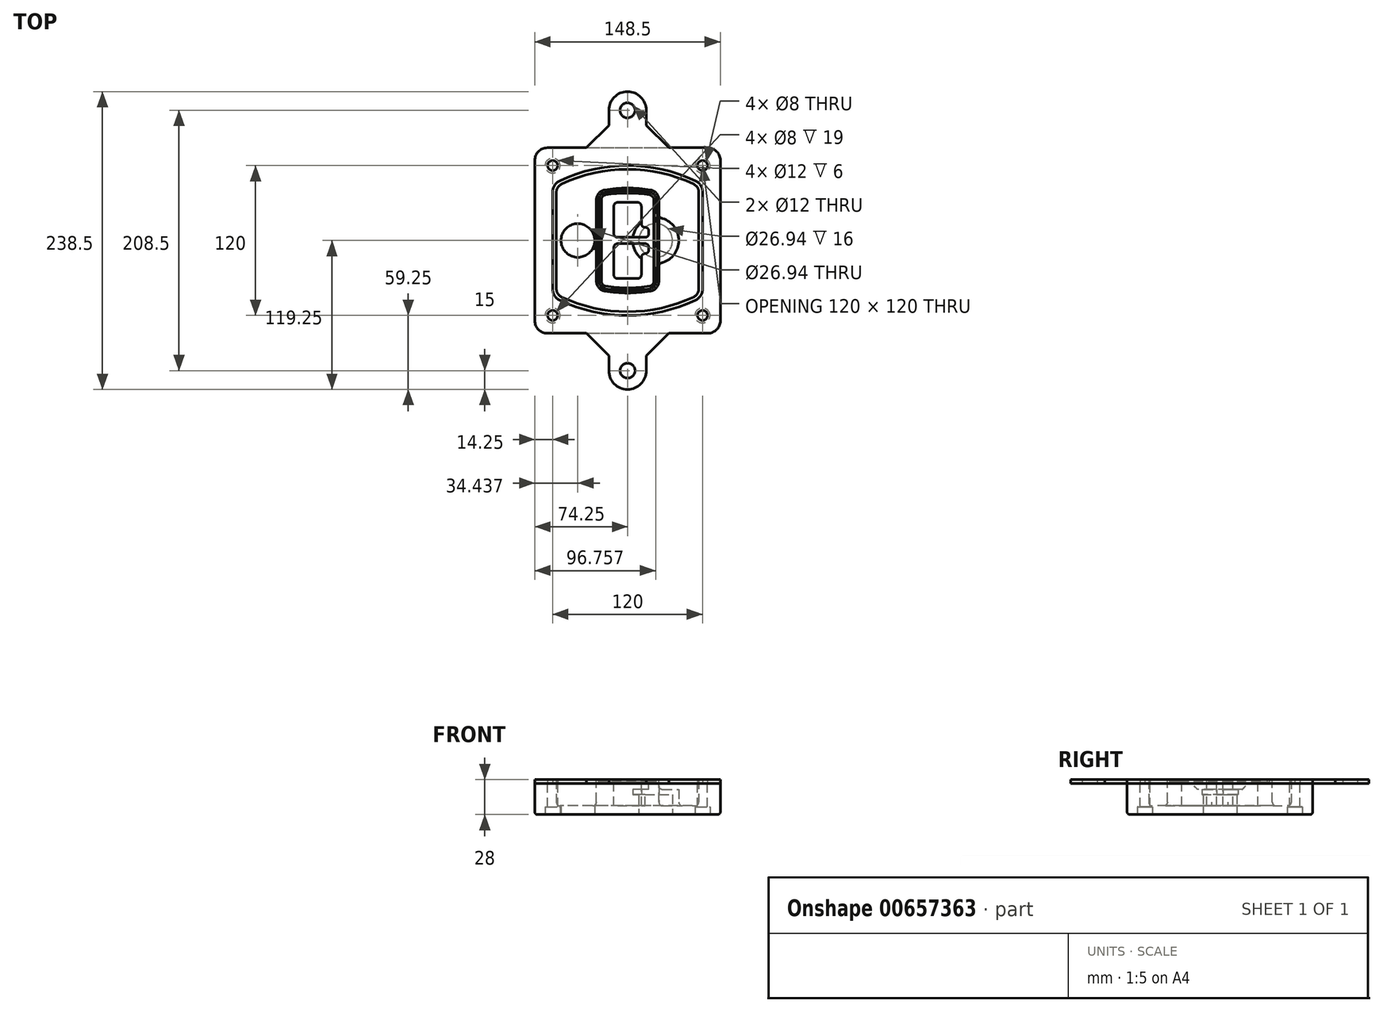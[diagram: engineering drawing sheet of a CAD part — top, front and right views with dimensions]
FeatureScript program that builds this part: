
annotation { "Feature Type Name" : "Feature", "Feature Type Description" : "" }
export const myFeature = defineFeature(function(context is Context, id is Id, definition is map)
    precondition{}
    {
        {
            var Q0;
            Q0=qCreatedBy(makeId("Top.planeOp"),FACE);
            var sketch = newSketch(context, id + "F0", { "sketchPlane" : qUnion([Q0])});
            skPoint(sketch, "E0.rect.middle", {"position": v(0, 0) * mm});
            skLineSegment(sketch, "E1.bottom", {"start": v(-64.25, -74.25) * mm, "end": v(64.25, -74.25) * mm});
            skLineSegment(sketch, "E1.top", {"start": v(-64.25, 74.25) * mm, "end": v(64.25, 74.25) * mm});
            skLineSegment(sketch, "E1.left", {"start": v(-74.25, -64.25) * mm, "end": v(-74.25, 64.25) * mm});
            skLineSegment(sketch, "E1.right", {"start": v(74.25, -64.25) * mm, "end": v(74.25, 64.25) * mm});
            skLineSegment(sketch, "E2", {"start": v(-74.25, 74.25) * mm, "end": v(74.25, -74.25) * mm, "construction": true});
            skLineSegment(sketch, "E3", {"start": v(74.25, 74.25) * mm, "end": v(-74.25, -74.25) * mm, "construction": true});
            skCircle(sketch, "E4", {"center": v(-60, 60) * mm, "radius": 4 * mm});
            skCircle(sketch, "E5", {"center": v(60, 60) * mm, "radius": 4 * mm});
            skCircle(sketch, "E6", {"center": v(60, -60) * mm, "radius": 4 * mm});
            skCircle(sketch, "E7", {"center": v(-60, -60) * mm, "radius": 4 * mm});
            skLineSegment(sketch, "E8", {"start": v(-60, 60) * mm, "end": v(60, 60) * mm, "construction": true});
            skLineSegment(sketch, "E9", {"start": v(60, 60) * mm, "end": v(60, -60) * mm, "construction": true});
            skLineSegment(sketch, "E10", {"start": v(60, -60) * mm, "end": v(-60, -60) * mm, "construction": true});
            skLineSegment(sketch, "E11", {"start": v(-60, -60) * mm, "end": v(-60, 60) * mm, "construction": true});
            skLineSegment(sketch, "E12", {"start": v(-60, 38.83) * mm, "end": v(-60, -38.83) * mm});
            skLineSegment(sketch, "E13", {"start": v(60, 38.83) * mm, "end": v(60, -38.83) * mm});
            skArc(sketch, "E14", {"start": v(54.26, 47.88) * mm, "mid": v(0, 60) * mm, "end": v(-54.26, 47.88) * mm});
            skArc(sketch, "E15", {"start": v(-54.26, -47.88) * mm, "mid": v(0, -60) * mm, "end": v(54.26, -47.88) * mm});
            skLineSegment(sketch, "E16", {"start": v(-60, 0) * mm, "end": v(60, 0) * mm, "construction": true});
            skPoint(sketch, "E17.visualSharp", {"position": v(-60, -45) * mm});
            skArc(sketch, "E17.filletArc", {"start": v(-60, -38.83) * mm, "mid": v(-58.44, -44.2) * mm, "end": v(-54.26, -47.88) * mm});
            skPoint(sketch, "E18.visualSharp", {"position": v(-60, 45) * mm});
            skArc(sketch, "E18.filletArc", {"start": v(-54.26, 47.88) * mm, "mid": v(-58.44, 44.2) * mm, "end": v(-60, 38.83) * mm});
            skPoint(sketch, "E19.visualSharp", {"position": v(60, 45) * mm});
            skArc(sketch, "E19.filletArc", {"start": v(60, 38.83) * mm, "mid": v(58.44, 44.2) * mm, "end": v(54.26, 47.88) * mm});
            skPoint(sketch, "E20.visualSharp", {"position": v(60, -45) * mm});
            skArc(sketch, "E20.filletArc", {"start": v(54.26, -47.88) * mm, "mid": v(58.44, -44.2) * mm, "end": v(60, -38.83) * mm});
            skPoint(sketch, "E21.visualSharp", {"position": v(-74.25, 74.25) * mm});
            skArc(sketch, "E21.filletArc", {"start": v(-64.25, 74.25) * mm, "mid": v(-71.32, 71.32) * mm, "end": v(-74.25, 64.25) * mm});
            skPoint(sketch, "E22.visualSharp", {"position": v(74.25, 74.25) * mm});
            skArc(sketch, "E22.filletArc", {"start": v(74.25, 64.25) * mm, "mid": v(71.32, 71.32) * mm, "end": v(64.25, 74.25) * mm});
            skPoint(sketch, "E23.visualSharp", {"position": v(74.25, -74.25) * mm});
            skArc(sketch, "E23.filletArc", {"start": v(64.25, -74.25) * mm, "mid": v(71.32, -71.32) * mm, "end": v(74.25, -64.25) * mm});
            skPoint(sketch, "E24.visualSharp", {"position": v(-74.25, -74.25) * mm});
            skArc(sketch, "E24.filletArc", {"start": v(-74.25, -64.25) * mm, "mid": v(-71.32, -71.32) * mm, "end": v(-64.25, -74.25) * mm});
            skArc(sketch, "E25.0", {"start": v(57, 38.83) * mm, "mid": v(55.9, 42.58) * mm, "end": v(52.98, 45.17) * mm});
            skLineSegment(sketch, "E25.1", {"start": v(57, 38.83) * mm, "end": v(57, -38.83) * mm});
            skArc(sketch, "E25.2", {"start": v(52.98, -45.17) * mm, "mid": v(55.9, -42.58) * mm, "end": v(57, -38.83) * mm});
            skArc(sketch, "E25.3", {"start": v(-52.98, -45.17) * mm, "mid": v(0, -57) * mm, "end": v(52.98, -45.17) * mm});
            skArc(sketch, "E25.4", {"start": v(-57, -38.83) * mm, "mid": v(-55.9, -42.58) * mm, "end": v(-52.98, -45.17) * mm});
            skArc(sketch, "E25.5", {"start": v(52.98, 45.17) * mm, "mid": v(0, 57) * mm, "end": v(-52.98, 45.17) * mm});
            skLineSegment(sketch, "E25.6", {"start": v(-57, 38.83) * mm, "end": v(-57, -38.83) * mm});
            skArc(sketch, "E25.7", {"start": v(-52.98, 45.17) * mm, "mid": v(-55.9, 42.58) * mm, "end": v(-57, 38.83) * mm});
            skArc(sketch, "E26.0", {"start": v(-55.96, 51.5) * mm, "mid": v(-61.82, 46.33) * mm, "end": v(-64, 38.83) * mm});
            skArc(sketch, "E26.1", {"start": v(55.96, 51.5) * mm, "mid": v(0, 64) * mm, "end": v(-55.96, 51.5) * mm});
            skArc(sketch, "E26.2", {"start": v(64, 38.83) * mm, "mid": v(61.82, 46.33) * mm, "end": v(55.96, 51.5) * mm});
            skLineSegment(sketch, "E26.3", {"start": v(64, 38.83) * mm, "end": v(64, -38.83) * mm});
            skArc(sketch, "E26.4", {"start": v(55.96, -51.5) * mm, "mid": v(61.82, -46.33) * mm, "end": v(64, -38.83) * mm});
            skLineSegment(sketch, "E26.5", {"start": v(-64, 38.83) * mm, "end": v(-64, -38.83) * mm});
            skArc(sketch, "E26.6", {"start": v(-55.96, -51.5) * mm, "mid": v(0, -64) * mm, "end": v(55.96, -51.5) * mm});
            skArc(sketch, "E26.7", {"start": v(-64, -38.83) * mm, "mid": v(-61.82, -46.33) * mm, "end": v(-55.96, -51.5) * mm});
            skLineSegment(sketch, "E27", {"start": v(0, 74.25) * mm, "end": v(0, 104.25) * mm, "construction": true});
            skCircle(sketch, "E28", {"center": v(0, 104.25) * mm, "radius": 6 * mm});
            skArc(sketch, "E29", {"start": v(-15, 104.25) * mm, "mid": v(0, 119.25) * mm, "end": v(15, 104.25) * mm});
            skLineSegment(sketch, "E30", {"start": v(-15, 104.25) * mm, "end": v(-15, 92.25) * mm});
            skLineSegment(sketch, "E31", {"start": v(15, 104.25) * mm, "end": v(15, 92.25) * mm});
            skLineSegment(sketch, "E32", {"start": v(15, 92.25) * mm, "end": v(33, 74.25) * mm});
            skLineSegment(sketch, "E33", {"start": v(-15, 92.25) * mm, "end": v(-33, 74.25) * mm});
            skCircle(sketch, "E34", {"center": v(0, -104.25) * mm, "radius": 6 * mm});
            skArc(sketch, "E35", {"start": v(15, -104.25) * mm, "mid": v(0, -119.25) * mm, "end": v(-15, -104.25) * mm});
            skLineSegment(sketch, "E36", {"start": v(-15, -104.25) * mm, "end": v(-15, -92.25) * mm});
            skLineSegment(sketch, "E37", {"start": v(15, -104.25) * mm, "end": v(15, -85.72) * mm});
            skLineSegment(sketch, "E38", {"start": v(15, -92.25) * mm, "end": v(33, -74.25) * mm});
            skLineSegment(sketch, "E39", {"start": v(-15, -92.25) * mm, "end": v(-33, -74.25) * mm});
            skLineSegment(sketch, "E40", {"start": v(0, -104.25) * mm, "end": v(0, -74.25) * mm, "construction": true});
            skSolve(sketch);
        }
        {
            var Q0;
            Q0=makeQuery(id+"F0.imprint","IMPRINT",FACE,{"disambiguationData":[TD([[makeQuery(id+"F0.imprint","IMPRINT",EDGE,{"derivedFrom":sQuery(id+"F0.wireOp",EDGE,"E1.bottom")}),1.0]])]});
            var Q1;
            Q1=makeQuery(id+"F0.imprint","IMPRINT",FACE,{"disambiguationData":[TD([[makeQuery(id+"F0.imprint","IMPRINT",EDGE,{"derivedFrom":sQuery(id+"F0.wireOp",EDGE,"E12")}),1.0]])]});
            var Q2;
            Q2=makeQuery(id+"F0.imprint","IMPRINT",FACE,{"disambiguationData":[TD([[makeQuery(id+"F0.imprint","IMPRINT",EDGE,{"derivedFrom":sQuery(id+"F0.wireOp",EDGE,"E25.0")}),1.0]])]});
            var Q3;
            Q3=makeQuery(id+"F0.imprint","IMPRINT",FACE,{"disambiguationData":[TD([[makeQuery(id+"F0.imprint","IMPRINT",EDGE,{"derivedFrom":sQuery(id+"F0.wireOp",EDGE,"E12")}),-1.0]])]});
            extrude(context, id + "F1", {"entities" : qUnion([Q0, Q1, Q2, Q3]), "oppositeDirection" : true, "depth" : 25 * mm});
        }
        {
            var Q0;
            Q0=makeQuery(id+"F0.imprint","IMPRINT",FACE,{"disambiguationData":[TD([[makeQuery(id+"F0.imprint","IMPRINT",EDGE,{"derivedFrom":sQuery(id+"F0.wireOp",EDGE,"E12")}),1.0]])]});
            extrude(context, id + "F2", {"entities" : qUnion([Q0]), "operationType" : NewBodyOperationType.ADD, "depth" : 3 * mm});
        }
        {
            var Q0;
            Q0=makeQuery(id+"F0.imprint","IMPRINT",FACE,{"disambiguationData":[TD([[makeQuery(id+"F0.imprint","IMPRINT",EDGE,{"derivedFrom":sQuery(id+"F0.wireOp",EDGE,"E25.0")}),1.0]])]});
            extrude(context, id + "F3", {"entities" : qUnion([Q0]), "operationType" : NewBodyOperationType.REMOVE, "oppositeDirection" : true, "depth" : 18 * mm});
        }
        {
            var Q0;
            Q0=makeQuery(id+"F2.opExtrude","CAP_FACE",FACE,{"disambiguationData":[OSD([sQuery(id+"F0.wireOp",EDGE,"E12"),sQuery(id+"F0.wireOp",EDGE,"E13"),sQuery(id+"F0.wireOp",EDGE,"E14"),sQuery(id+"F0.wireOp",EDGE,"E15"),sQuery(id+"F0.wireOp",EDGE,"E17.filletArc"),sQuery(id+"F0.wireOp",EDGE,"E18.filletArc"),sQuery(id+"F0.wireOp",EDGE,"E19.filletArc"),sQuery(id+"F0.wireOp",EDGE,"E20.filletArc"),sQuery(id+"F0.wireOp",EDGE,"E25.0"),sQuery(id+"F0.wireOp",EDGE,"E25.1"),sQuery(id+"F0.wireOp",EDGE,"E25.2"),sQuery(id+"F0.wireOp",EDGE,"E25.3"),sQuery(id+"F0.wireOp",EDGE,"E25.4"),sQuery(id+"F0.wireOp",EDGE,"E25.5"),sQuery(id+"F0.wireOp",EDGE,"E25.6"),sQuery(id+"F0.wireOp",EDGE,"E25.7")])],"isStart":false});
            var sketch = newSketch(context, id + "F4", { "sketchPlane" : qUnion([Q0])});
            skArc(sketch, "E41.0", {"start": v(-18.34, -40.45) * mm, "mid": v(0, -42) * mm, "end": v(18.34, -40.45) * mm});
            skArc(sketch, "E42.0", {"start": v(18.34, 40.45) * mm, "mid": v(0, 42) * mm, "end": v(-18.34, 40.45) * mm});
            skLineSegment(sketch, "E43", {"start": v(-25, 32.57) * mm, "end": v(-25, -32.57) * mm});
            skLineSegment(sketch, "E44", {"start": v(25, 32.57) * mm, "end": v(25, -32.57) * mm});
            skLineSegment(sketch, "E45", {"start": v(-25, 39.1) * mm, "end": v(25, 39.1) * mm, "construction": true});
            skLineSegment(sketch, "E46", {"start": v(-25, -39.1) * mm, "end": v(25, -39.1) * mm, "construction": true});
            skPoint(sketch, "E47.visualSharp", {"position": v(-25, 39.1) * mm});
            skArc(sketch, "E47.filletArc", {"start": v(-18.34, 40.45) * mm, "mid": v(-23.11, 37.73) * mm, "end": v(-25, 32.57) * mm});
            skPoint(sketch, "E48.visualSharp", {"position": v(25, 39.1) * mm});
            skArc(sketch, "E48.filletArc", {"start": v(25, 32.57) * mm, "mid": v(23.11, 37.73) * mm, "end": v(18.34, 40.45) * mm});
            skPoint(sketch, "E49.visualSharp", {"position": v(25, -39.1) * mm});
            skArc(sketch, "E49.filletArc", {"start": v(18.34, -40.45) * mm, "mid": v(23.11, -37.73) * mm, "end": v(25, -32.57) * mm});
            skPoint(sketch, "E50.visualSharp", {"position": v(-25, -39.1) * mm});
            skArc(sketch, "E50.filletArc", {"start": v(-25, -32.57) * mm, "mid": v(-23.11, -37.73) * mm, "end": v(-18.34, -40.45) * mm});
            skArc(sketch, "E51.0", {"start": v(52.98, 45.17) * mm, "mid": v(0, 57) * mm, "end": v(-52.98, 45.17) * mm});
            skArc(sketch, "E51.1", {"start": v(-52.98, 45.17) * mm, "mid": v(-55.9, 42.58) * mm, "end": v(-57, 38.83) * mm});
            skLineSegment(sketch, "E51.2", {"start": v(-57, 38.83) * mm, "end": v(-57, -38.83) * mm});
            skArc(sketch, "E51.3", {"start": v(-57, -38.83) * mm, "mid": v(-55.9, -42.58) * mm, "end": v(-52.98, -45.17) * mm});
            skArc(sketch, "E51.4", {"start": v(-52.98, -45.17) * mm, "mid": v(0, -57) * mm, "end": v(52.98, -45.17) * mm});
            skArc(sketch, "E51.5", {"start": v(52.98, -45.17) * mm, "mid": v(55.9, -42.58) * mm, "end": v(57, -38.83) * mm});
            skLineSegment(sketch, "E51.6", {"start": v(57, 38.83) * mm, "end": v(57, -38.83) * mm});
            skArc(sketch, "E51.7", {"start": v(57, 38.83) * mm, "mid": v(55.9, 42.58) * mm, "end": v(52.98, 45.17) * mm});
            skLineSegment(sketch, "E52.0", {"start": v(23, 32.57) * mm, "end": v(23, -32.57) * mm});
            skArc(sketch, "E52.1", {"start": v(18, -38.48) * mm, "mid": v(21.58, -36.44) * mm, "end": v(23, -32.57) * mm});
            skArc(sketch, "E52.2", {"start": v(-18, -38.48) * mm, "mid": v(0, -40) * mm, "end": v(18, -38.48) * mm});
            skArc(sketch, "E52.3", {"start": v(-23, -32.57) * mm, "mid": v(-21.58, -36.44) * mm, "end": v(-18, -38.48) * mm});
            skLineSegment(sketch, "E52.4", {"start": v(-23, 32.57) * mm, "end": v(-23, -32.57) * mm});
            skArc(sketch, "E52.5", {"start": v(23, 32.57) * mm, "mid": v(21.58, 36.44) * mm, "end": v(18, 38.48) * mm});
            skArc(sketch, "E52.6", {"start": v(-18, 38.48) * mm, "mid": v(-21.58, 36.44) * mm, "end": v(-23, 32.57) * mm});
            skArc(sketch, "E52.7", {"start": v(18, 38.48) * mm, "mid": v(0, 40) * mm, "end": v(-18, 38.48) * mm});
            skArc(sketch, "E53.0", {"start": v(21, 32.57) * mm, "mid": v(20.06, 35.15) * mm, "end": v(17.67, 36.5) * mm});
            skLineSegment(sketch, "E53.1", {"start": v(21, 32.57) * mm, "end": v(21, -32.57) * mm});
            skArc(sketch, "E53.2", {"start": v(17.67, -36.5) * mm, "mid": v(20.06, -35.15) * mm, "end": v(21, -32.57) * mm});
            skArc(sketch, "E53.3", {"start": v(-17.67, -36.5) * mm, "mid": v(0, -38) * mm, "end": v(17.67, -36.5) * mm});
            skArc(sketch, "E53.4", {"start": v(-21, -32.57) * mm, "mid": v(-20.06, -35.15) * mm, "end": v(-17.67, -36.5) * mm});
            skArc(sketch, "E53.5", {"start": v(17.67, 36.5) * mm, "mid": v(0, 38) * mm, "end": v(-17.67, 36.5) * mm});
            skLineSegment(sketch, "E53.6", {"start": v(-21, 32.57) * mm, "end": v(-21, -32.57) * mm});
            skArc(sketch, "E53.7", {"start": v(-17.67, 36.5) * mm, "mid": v(-20.06, 35.15) * mm, "end": v(-21, 32.57) * mm});
            skLineSegment(sketch, "E54", {"start": v(-25, 0) * mm, "end": v(25, 0) * mm, "construction": true});
            skLineSegment(sketch, "E55", {"start": v(-11, 5.5) * mm, "end": v(-11, 27.5) * mm});
            skLineSegment(sketch, "E56", {"start": v(-8, 30.5) * mm, "end": v(8, 30.5) * mm});
            skLineSegment(sketch, "E57", {"start": v(11, 27.5) * mm, "end": v(11, 13.5) * mm});
            skLineSegment(sketch, "E58", {"start": v(14, 10.5) * mm, "end": v(14, 10.5) * mm});
            skLineSegment(sketch, "E59", {"start": v(17, 7.5) * mm, "end": v(17, 5.5) * mm});
            skLineSegment(sketch, "E60", {"start": v(14, 2.5) * mm, "end": v(-8, 2.5) * mm});
            skPoint(sketch, "E61.visualSharp", {"position": v(-11, 30.5) * mm});
            skArc(sketch, "E61.filletArc", {"start": v(-8, 30.5) * mm, "mid": v(-10.12, 29.62) * mm, "end": v(-11, 27.5) * mm});
            skPoint(sketch, "E62.visualSharp", {"position": v(11, 30.5) * mm});
            skArc(sketch, "E62.filletArc", {"start": v(11, 27.5) * mm, "mid": v(10.12, 29.62) * mm, "end": v(8, 30.5) * mm});
            skPoint(sketch, "E63.visualSharp", {"position": v(11, 10.5) * mm});
            skArc(sketch, "E63.filletArc", {"start": v(11, 13.5) * mm, "mid": v(11.88, 11.38) * mm, "end": v(14, 10.5) * mm});
            skPoint(sketch, "E64.visualSharp", {"position": v(17, 10.5) * mm});
            skArc(sketch, "E64.filletArc", {"start": v(17, 7.5) * mm, "mid": v(16.12, 9.62) * mm, "end": v(14, 10.5) * mm});
            skPoint(sketch, "E65.visualSharp", {"position": v(17, 2.5) * mm});
            skArc(sketch, "E65.filletArc", {"start": v(14, 2.5) * mm, "mid": v(16.12, 3.38) * mm, "end": v(17, 5.5) * mm});
            skPoint(sketch, "E66.visualSharp", {"position": v(-11, 2.5) * mm});
            skArc(sketch, "E66.filletArc", {"start": v(-11, 5.5) * mm, "mid": v(-10.12, 3.38) * mm, "end": v(-8, 2.5) * mm});
            skLineSegment(sketch, "E67.0.MirrorCS", {"start": v(14, -2.5) * mm, "end": v(-8, -2.5) * mm});
            skArc(sketch, "E68.0.MirrorCS", {"start": v(-11, -5.5) * mm, "mid": v(-10.12, -3.38) * mm, "end": v(-8, -2.5) * mm});
            skLineSegment(sketch, "E69.0.MirrorCS", {"start": v(-11, -5.5) * mm, "end": v(-11, -27.5) * mm});
            skArc(sketch, "E70.0.MirrorCS", {"start": v(-8, -30.5) * mm, "mid": v(-10.12, -29.62) * mm, "end": v(-11, -27.5) * mm});
            skLineSegment(sketch, "E71.0.MirrorCS", {"start": v(-8, -30.5) * mm, "end": v(8, -30.5) * mm});
            skArc(sketch, "E72.0.MirrorCS", {"start": v(11, -27.5) * mm, "mid": v(10.12, -29.62) * mm, "end": v(8, -30.5) * mm});
            skLineSegment(sketch, "E73.0.MirrorCS", {"start": v(11, -27.5) * mm, "end": v(11, -13.5) * mm});
            skArc(sketch, "E74.0.MirrorCS", {"start": v(11, -13.5) * mm, "mid": v(11.88, -11.38) * mm, "end": v(14, -10.5) * mm});
            skArc(sketch, "E75.0.MirrorCS", {"start": v(17, -7.5) * mm, "mid": v(16.12, -9.62) * mm, "end": v(14, -10.5) * mm});
            skLineSegment(sketch, "E76.0.MirrorCS", {"start": v(17, -7.5) * mm, "end": v(17, -5.5) * mm});
            skArc(sketch, "E77.0.MirrorCS", {"start": v(14, -2.5) * mm, "mid": v(16.12, -3.38) * mm, "end": v(17, -5.5) * mm});
            skSolve(sketch);
        }
        {
            var Q0;
            Q0=makeQuery(id+"F4.imprint","IMPRINT",FACE,{"disambiguationData":[TD([[makeQuery(id+"F4.imprint","IMPRINT",EDGE,{"derivedFrom":sQuery(id+"F4.wireOp",EDGE,"E41.0")}),1.0]])]});
            var Q1;
            Q1=makeQuery(id+"F4.imprint","IMPRINT",FACE,{"disambiguationData":[TD([[makeQuery(id+"F4.imprint","IMPRINT",EDGE,{"derivedFrom":sQuery(id+"F4.wireOp",EDGE,"E52.0")}),-1.0]])]});
            var Q2;
            Q2=makeQuery(id+"F4.imprint","IMPRINT",FACE,{"disambiguationData":[TD([[makeQuery(id+"F4.imprint","IMPRINT",EDGE,{"derivedFrom":sQuery(id+"F4.wireOp",EDGE,"E53.0")}),1.0]])]});
            extrude(context, id + "F5", {"entities" : qUnion([Q0, Q1, Q2]), "operationType" : NewBodyOperationType.ADD, "endBound" : BoundingType.UP_TO_NEXT, "oppositeDirection" : true, "depth" : 25 * mm});
        }
        {
            var Q0;
            Q0=makeQuery(id+"F4.imprint","IMPRINT",FACE,{"disambiguationData":[TD([[makeQuery(id+"F4.imprint","IMPRINT",EDGE,{"derivedFrom":sQuery(id+"F4.wireOp",EDGE,"E52.0")}),-1.0]])]});
            extrude(context, id + "F6", {"entities" : qUnion([Q0]), "operationType" : NewBodyOperationType.REMOVE, "oppositeDirection" : true, "depth" : 2 * mm});
        }
        {
            var Q0;
            Q0=makeQuery(id+"F1.opExtrude","CAP_FACE",FACE,{"disambiguationData":[OSD([sQuery(id+"F0.wireOp",EDGE,"E1.bottom"),sQuery(id+"F0.wireOp",EDGE,"E1.top"),sQuery(id+"F0.wireOp",EDGE,"E1.left"),sQuery(id+"F0.wireOp",EDGE,"E1.right"),sQuery(id+"F0.wireOp",EDGE,"E4"),sQuery(id+"F0.wireOp",EDGE,"E5"),sQuery(id+"F0.wireOp",EDGE,"E6"),sQuery(id+"F0.wireOp",EDGE,"E7"),sQuery(id+"F0.wireOp",EDGE,"E21.filletArc"),sQuery(id+"F0.wireOp",EDGE,"E22.filletArc"),sQuery(id+"F0.wireOp",EDGE,"E23.filletArc"),sQuery(id+"F0.wireOp",EDGE,"E24.filletArc")])],"isStart":false});
            var sketch = newSketch(context, id + "F7", { "sketchPlane" : qUnion([Q0])});
            skCircle(sketch, "E78", {"center": v(22.5, 0) * mm, "radius": 13.47 * mm});
            skCircle(sketch, "E79", {"center": v(-39.81, 0) * mm, "radius": 13.47 * mm});
            skLineSegment(sketch, "E80", {"start": v(74.25, 0) * mm, "end": v(-74.25, 0) * mm});
            skCircle(sketch, "E81", {"center": v(22.5, 0) * mm, "radius": 18.47 * mm});
            skCircle(sketch, "E82", {"center": v(60, -60) * mm, "radius": 6 * mm});
            skCircle(sketch, "E83", {"center": v(-60, -60) * mm, "radius": 6 * mm});
            skCircle(sketch, "E84", {"center": v(-60, 60) * mm, "radius": 6 * mm});
            skCircle(sketch, "E85", {"center": v(60, 60) * mm, "radius": 6 * mm});
            skSolve(sketch);
        }
        {
            var Q0;
            {var subQ1=sQuery(id+"F7.wireOp",EDGE,"E80");var subQ4=sQuery(id+"F7.wireOp",EDGE,"E78");var subQ6=makeQuery(id+"F7.imprint","INTERSECT",VERTEX,{"disambiguationData":[OD(0.0)],"derivedFrom":[subQ4,subQ1]});Q0=makeQuery(id+"F7.imprint","IMPRINT",FACE,{"disambiguationData":[TD([[makeQuery(id+"F7.imprint","IMPRINT",EDGE,{"disambiguationData":[TD([[subQ6,-1.0]])],"derivedFrom":subQ4}),-1.0]])]});}
            var Q1;
            {var subQ0=sQuery(id+"F7.wireOp",EDGE,"E80");var subQ1=sQuery(id+"F7.wireOp",EDGE,"E78");var subQ3=makeQuery(id+"F7.imprint","INTERSECT",VERTEX,{"disambiguationData":[OD(0.0)],"derivedFrom":[subQ1,subQ0]});Q1=makeQuery(id+"F7.imprint","IMPRINT",FACE,{"disambiguationData":[TD([[makeQuery(id+"F7.imprint","IMPRINT",EDGE,{"disambiguationData":[TD([[subQ3,-1.0]])],"derivedFrom":subQ1}),1.0]])]});}
            var Q2;
            {var subQ0=sQuery(id+"F7.wireOp",EDGE,"E80");var subQ1=sQuery(id+"F7.wireOp",EDGE,"E78");var subQ3=makeQuery(id+"F7.imprint","INTERSECT",VERTEX,{"disambiguationData":[OD(0.0)],"derivedFrom":[subQ1,subQ0]});Q2=makeQuery(id+"F7.imprint","IMPRINT",FACE,{"disambiguationData":[TD([[makeQuery(id+"F7.imprint","IMPRINT",EDGE,{"disambiguationData":[TD([[subQ3,1.0]])],"derivedFrom":subQ1}),1.0]])]});}
            var Q3;
            {var subQ1=sQuery(id+"F7.wireOp",EDGE,"E80");var subQ4=sQuery(id+"F7.wireOp",EDGE,"E78");var subQ6=makeQuery(id+"F7.imprint","INTERSECT",VERTEX,{"disambiguationData":[OD(0.0)],"derivedFrom":[subQ4,subQ1]});Q3=makeQuery(id+"F7.imprint","IMPRINT",FACE,{"disambiguationData":[TD([[makeQuery(id+"F7.imprint","IMPRINT",EDGE,{"disambiguationData":[TD([[subQ6,1.0]])],"derivedFrom":subQ4}),-1.0]])]});}
            extrude(context, id + "F8", {"entities" : qUnion([Q0, Q1, Q2, Q3]), "operationType" : NewBodyOperationType.ADD, "oppositeDirection" : true, "depth" : 20 * mm});
        }
        {
            var Q0;
            {var subQ0=sQuery(id+"F7.wireOp",EDGE,"E80");var subQ1=sQuery(id+"F7.wireOp",EDGE,"E78");var subQ3=makeQuery(id+"F7.imprint","INTERSECT",VERTEX,{"disambiguationData":[OD(0.0)],"derivedFrom":[subQ1,subQ0]});Q0=makeQuery(id+"F7.imprint","IMPRINT",FACE,{"disambiguationData":[TD([[makeQuery(id+"F7.imprint","IMPRINT",EDGE,{"disambiguationData":[TD([[subQ3,-1.0]])],"derivedFrom":subQ1}),1.0]])]});}
            var Q1;
            {var subQ0=sQuery(id+"F7.wireOp",EDGE,"E80");var subQ1=sQuery(id+"F7.wireOp",EDGE,"E78");var subQ3=makeQuery(id+"F7.imprint","INTERSECT",VERTEX,{"disambiguationData":[OD(0.0)],"derivedFrom":[subQ1,subQ0]});Q1=makeQuery(id+"F7.imprint","IMPRINT",FACE,{"disambiguationData":[TD([[makeQuery(id+"F7.imprint","IMPRINT",EDGE,{"disambiguationData":[TD([[subQ3,1.0]])],"derivedFrom":subQ1}),1.0]])]});}
            var Q2;
            Q2 = qSketchRegion(id + "F17", true);
            extrude(context, id + "F9", {"entities" : qUnion([Q0, Q1, Q2]), "operationType" : NewBodyOperationType.REMOVE, "oppositeDirection" : true, "depth" : 16 * mm, "offsetDistance" : 25 * mm});
        }
        {
            var Q0;
            {var subQ0=sQuery(id+"F7.wireOp",EDGE,"E80");var subQ1=sQuery(id+"F7.wireOp",EDGE,"E79");var subQ3=makeQuery(id+"F7.imprint","INTERSECT",VERTEX,{"disambiguationData":[OD(0.0)],"derivedFrom":[subQ1,subQ0]});Q0=makeQuery(id+"F7.imprint","IMPRINT",FACE,{"disambiguationData":[TD([[makeQuery(id+"F7.imprint","IMPRINT",EDGE,{"disambiguationData":[TD([[subQ3,-1.0]])],"derivedFrom":subQ1}),1.0]])]});}
            var Q1;
            {var subQ0=sQuery(id+"F7.wireOp",EDGE,"E80");var subQ1=sQuery(id+"F7.wireOp",EDGE,"E79");var subQ3=makeQuery(id+"F7.imprint","INTERSECT",VERTEX,{"disambiguationData":[OD(0.0)],"derivedFrom":[subQ1,subQ0]});Q1=makeQuery(id+"F7.imprint","IMPRINT",FACE,{"disambiguationData":[TD([[makeQuery(id+"F7.imprint","IMPRINT",EDGE,{"disambiguationData":[TD([[subQ3,1.0]])],"derivedFrom":subQ1}),1.0]])]});}
            extrude(context, id + "F10", {"entities" : qUnion([Q0, Q1]), "operationType" : NewBodyOperationType.REMOVE, "oppositeDirection" : true, "depth" : 25 * mm});
        }
        {
            var Q0;
            Q0=makeQuery(id+"F7.imprint","IMPRINT",FACE,{"disambiguationData":[TD([[makeQuery(id+"F7.imprint","IMPRINT",EDGE,{"derivedFrom":sQuery(id+"F7.wireOp",EDGE,"E82")}),1.0]])]});
            var Q1;
            Q1=makeQuery(id+"F7.imprint","IMPRINT",FACE,{"disambiguationData":[TD([[makeQuery(id+"F7.imprint","IMPRINT",EDGE,{"derivedFrom":makeQuery(id+"F1.opExtrude","CAP_EDGE",EDGE,{"disambiguationData":[OSD([sQuery(id+"F0.wireOp",EDGE,"E5")])],"isStart":false})}),-1.0]])]});
            var Q2;
            Q2=makeQuery(id+"F7.imprint","IMPRINT",FACE,{"disambiguationData":[TD([[makeQuery(id+"F7.imprint","IMPRINT",EDGE,{"derivedFrom":sQuery(id+"F7.wireOp",EDGE,"E83")}),1.0]])]});
            var Q3;
            Q3=makeQuery(id+"F7.imprint","IMPRINT",FACE,{"disambiguationData":[TD([[makeQuery(id+"F7.imprint","IMPRINT",EDGE,{"derivedFrom":makeQuery(id+"F1.opExtrude","CAP_EDGE",EDGE,{"disambiguationData":[OSD([sQuery(id+"F0.wireOp",EDGE,"E4")])],"isStart":false})}),-1.0]])]});
            var Q4;
            Q4=makeQuery(id+"F7.imprint","IMPRINT",FACE,{"disambiguationData":[TD([[makeQuery(id+"F7.imprint","IMPRINT",EDGE,{"derivedFrom":sQuery(id+"F7.wireOp",EDGE,"E84")}),1.0]])]});
            var Q5;
            Q5=makeQuery(id+"F7.imprint","IMPRINT",FACE,{"disambiguationData":[TD([[makeQuery(id+"F7.imprint","IMPRINT",EDGE,{"derivedFrom":makeQuery(id+"F1.opExtrude","CAP_EDGE",EDGE,{"disambiguationData":[OSD([sQuery(id+"F0.wireOp",EDGE,"E7")])],"isStart":false})}),-1.0]])]});
            var Q6;
            Q6=makeQuery(id+"F7.imprint","IMPRINT",FACE,{"disambiguationData":[TD([[makeQuery(id+"F7.imprint","IMPRINT",EDGE,{"derivedFrom":sQuery(id+"F7.wireOp",EDGE,"E85")}),1.0]])]});
            var Q7;
            Q7=makeQuery(id+"F7.imprint","IMPRINT",FACE,{"disambiguationData":[TD([[makeQuery(id+"F7.imprint","IMPRINT",EDGE,{"derivedFrom":makeQuery(id+"F1.opExtrude","CAP_EDGE",EDGE,{"disambiguationData":[OSD([sQuery(id+"F0.wireOp",EDGE,"E6")])],"isStart":false})}),-1.0]])]});
            extrude(context, id + "F11", {"entities" : qUnion([Q0, Q1, Q2, Q3, Q4, Q5, Q6, Q7]), "operationType" : NewBodyOperationType.REMOVE, "oppositeDirection" : true, "depth" : 6 * mm});
        }
        {
            var Q0;
            Q0=makeQuery(id+"F9.boolean.opBoolean","COPY",FACE,{"derivedFrom":makeQuery(id+"F9.opExtrude","CAP_FACE",FACE,{"disambiguationData":[OSD([sQuery(id+"F7.wireOp",EDGE,"E78")])],"isStart":false})});
            var sketch = newSketch(context, id + "F12", { "sketchPlane" : qUnion([Q0])});
            skArc(sketch, "E86.0", {"start": v(11, 14.45) * mm, "mid": v(6.45, 9.13) * mm, "end": v(4.2, 2.5) * mm});
            skArc(sketch, "E86.1", {"start": v(4.2, -2.5) * mm, "mid": v(6.45, -9.13) * mm, "end": v(11, -14.45) * mm});
            skLineSegment(sketch, "E87", {"start": v(4.2, -2.5) * mm, "end": v(14, -2.5) * mm});
            skLineSegment(sketch, "E88.0", {"start": v(14, 2.5) * mm, "end": v(4.2, 2.5) * mm});
            skArc(sketch, "E88.1", {"start": v(14, 2.5) * mm, "mid": v(16.12, 3.38) * mm, "end": v(17, 5.5) * mm});
            skLineSegment(sketch, "E88.2", {"start": v(17, 7.5) * mm, "end": v(17, 5.5) * mm});
            skArc(sketch, "E88.3", {"start": v(17, 7.5) * mm, "mid": v(16.12, 9.62) * mm, "end": v(14, 10.5) * mm});
            skArc(sketch, "E88.4", {"start": v(11, 13.5) * mm, "mid": v(11.88, 11.38) * mm, "end": v(14, 10.5) * mm});
            skLineSegment(sketch, "E88.5", {"start": v(11, 14.45) * mm, "end": v(11, 13.5) * mm});
            skLineSegment(sketch, "E88.7", {"start": v(14, -2.5) * mm, "end": v(4.2, -2.5) * mm});
            skArc(sketch, "E88.8", {"start": v(14, -2.5) * mm, "mid": v(16.12, -3.38) * mm, "end": v(17, -5.5) * mm});
            skLineSegment(sketch, "E88.9", {"start": v(17, -7.5) * mm, "end": v(17, -5.5) * mm});
            skArc(sketch, "E88.10", {"start": v(17, -7.5) * mm, "mid": v(16.12, -9.62) * mm, "end": v(14, -10.5) * mm});
            skArc(sketch, "E88.11", {"start": v(11, -13.5) * mm, "mid": v(11.88, -11.38) * mm, "end": v(14, -10.5) * mm});
            skLineSegment(sketch, "E88.12", {"start": v(11, -14.45) * mm, "end": v(11, -13.5) * mm});
            skPoint(sketch, "E89.orphan", {"position": v(11, -27.5) * mm});
            skPoint(sketch, "E90.orphan", {"position": v(-8, -2.5) * mm});
            skPoint(sketch, "E91.orphan", {"position": v(-8, 2.5) * mm});
            skPoint(sketch, "E92.orphan", {"position": v(11, 27.5) * mm});
            skSolve(sketch);
        }
        {
            var Q0;
            {var subQ7=sQuery(id+"F12.wireOp",EDGE,"E86.0");var subQ14=sQuery(id+"F12.wireOp",EDGE,"E86.1");var subQ16=sQuery(id+"F12.wireOp",EDGE,"E88.1");var subQ18=sQuery(id+"F12.wireOp",EDGE,"E88.8");Q0=qUnion([makeQuery(id+"F12.imprint","IMPRINT",FACE,{"disambiguationData":[TD([[makeQuery(id+"F12.imprint","IMPRINT",EDGE,{"derivedFrom":subQ7}),1.0]])]}),makeQuery(id+"F12.imprint","IMPRINT",FACE,{"disambiguationData":[TD([[makeQuery(id+"F12.imprint","IMPRINT",EDGE,{"derivedFrom":subQ14}),1.0]])]}),makeQuery(id+"F12.imprint","IMPRINT",FACE,{"disambiguationData":[TD([[makeQuery(id+"F12.imprint","IMPRINT",EDGE,{"derivedFrom":subQ16}),1.0]])]}),makeQuery(id+"F12.imprint","IMPRINT",FACE,{"disambiguationData":[TD([[makeQuery(id+"F12.imprint","IMPRINT",EDGE,{"derivedFrom":subQ18}),-1.0]])]})]);}
            var Q1;
            Q1=makeQuery(id+"F5.boolean.opBoolean","SPLIT",FACE,{"disambiguationData":[TD([makeQuery(id+"F5.opExtrude","SWEPT_FACE",FACE,{"disambiguationData":[OSD([sQuery(id+"F4.wireOp",EDGE,"E55")])]})])],"derivedFrom":makeQuery(id+"F3.boolean.opBoolean","COPY",FACE,{"derivedFrom":makeQuery(id+"F3.opExtrude","CAP_FACE",FACE,{"disambiguationData":[OSD([sQuery(id+"F0.wireOp",EDGE,"E25.0"),sQuery(id+"F0.wireOp",EDGE,"E25.1"),sQuery(id+"F0.wireOp",EDGE,"E25.2"),sQuery(id+"F0.wireOp",EDGE,"E25.3"),sQuery(id+"F0.wireOp",EDGE,"E25.4"),sQuery(id+"F0.wireOp",EDGE,"E25.5"),sQuery(id+"F0.wireOp",EDGE,"E25.6"),sQuery(id+"F0.wireOp",EDGE,"E25.7")])],"isStart":false})})});
            extrude(context, id + "F13", {"entities" : qUnion([Q0]), "operationType" : NewBodyOperationType.REMOVE, "endBound" : BoundingType.UP_TO_SURFACE, "endBoundEntityFace" : qUnion([Q1]), "depth" : 25 * mm});
        }
        {
            var Q0;
            Q0=makeQuery(id+"F3.boolean.opBoolean","COPY",EDGE,{"derivedFrom":makeQuery(id+"F3.opExtrude","CAP_EDGE",EDGE,{"disambiguationData":[OSD([sQuery(id+"F0.wireOp",EDGE,"E25.6")])],"isStart":false})});
            var Q1;
            Q1=makeQuery(id+"F8.boolean.opBoolean","INTERSECT",EDGE,{"derivedFrom":[makeQuery(id+"F5.opExtrude","SWEPT_FACE",FACE,{"disambiguationData":[OSD([sQuery(id+"F4.wireOp",EDGE,"E44")])]}),makeQuery(id+"F8.opExtrude","CAP_FACE",FACE,{"disambiguationData":[OSD([sQuery(id+"F7.wireOp",EDGE,"E81")])],"isStart":false})]});
            var Q2;
            Q2=makeQuery(id+"F8.boolean.opBoolean","INTERSECT",EDGE,{"disambiguationData":[OD(1.0)],"derivedFrom":[makeQuery(id+"F5.opExtrude","SWEPT_FACE",FACE,{"disambiguationData":[OSD([sQuery(id+"F4.wireOp",EDGE,"E44")])]}),makeQuery(id+"F8.opExtrude","SWEPT_FACE",FACE,{"disambiguationData":[OSD([sQuery(id+"F7.wireOp",EDGE,"E81")])]})]});
            var Q3;
            {var subQ0=sQuery(id+"F4.wireOp",EDGE,"E44");Q3=makeQuery(id+"F8.boolean.opBoolean","SPLIT",EDGE,{"disambiguationData":[TD([makeQuery(id+"F5.opExtrude","SWEPT_FACE",FACE,{"disambiguationData":[OSD([sQuery(id+"F4.wireOp",EDGE,"E49.filletArc")])]})])],"derivedFrom":makeQuery(id+"F5.opExtrude","CAP_EDGE",EDGE,{"disambiguationData":[OSD([subQ0])],"isStart":false})});}
            var Q4;
            {var subQ0=sQuery(id+"F0.wireOp",EDGE,"E25.7");var subQ1=sQuery(id+"F0.wireOp",EDGE,"E25.1");var subQ2=sQuery(id+"F0.wireOp",EDGE,"E25.6");var subQ3=sQuery(id+"F0.wireOp",EDGE,"E25.5");var subQ4=sQuery(id+"F0.wireOp",EDGE,"E25.4");var subQ5=sQuery(id+"F0.wireOp",EDGE,"E25.0");var subQ6=sQuery(id+"F0.wireOp",EDGE,"E25.2");var subQ7=sQuery(id+"F0.wireOp",EDGE,"E25.3");Q4=makeQuery(id+"F8.boolean.opBoolean","INTERSECT",EDGE,{"derivedFrom":[makeQuery(id+"F5.boolean.opBoolean","SPLIT",FACE,{"disambiguationData":[TD([makeQuery(id+"F2.opExtrude","SWEPT_FACE",FACE,{"disambiguationData":[OSD([subQ5])]})])],"derivedFrom":makeQuery(id+"F3.boolean.opBoolean","COPY",FACE,{"derivedFrom":makeQuery(id+"F3.opExtrude","CAP_FACE",FACE,{"disambiguationData":[OSD([subQ5,subQ1,subQ6,subQ7,subQ4,subQ3,subQ2,subQ0])],"isStart":false})})}),makeQuery(id+"F8.opExtrude","SWEPT_FACE",FACE,{"disambiguationData":[OSD([sQuery(id+"F7.wireOp",EDGE,"E81")])]})]});}
            var Q5;
            Q5=makeQuery(id+"F8.boolean.opBoolean","INTERSECT",EDGE,{"disambiguationData":[OD(0.0)],"derivedFrom":[makeQuery(id+"F5.opExtrude","SWEPT_FACE",FACE,{"disambiguationData":[OSD([sQuery(id+"F4.wireOp",EDGE,"E44")])]}),makeQuery(id+"F8.opExtrude","SWEPT_FACE",FACE,{"disambiguationData":[OSD([sQuery(id+"F7.wireOp",EDGE,"E81")])]})]});
            fillet(context, id + "F14", {"entities" : qUnion([Q0, Q1, Q2, Q3, Q4, Q5]), "radius" : 3 * mm, "tangentPropagation" : true, "allowEdgeOverflow" : false});
        }
        {
            var Q0;
            Q0=makeQuery(id+"F1.opExtrude","CAP_EDGE",EDGE,{"disambiguationData":[OSD([sQuery(id+"F0.wireOp",EDGE,"E1.bottom")])],"isStart":false});
            fillet(context, id + "F15", {"entities" : qUnion([Q0]), "radius" : 2 * mm, "tangentPropagation" : true, "allowEdgeOverflow" : false});
        }
        {
            var Q0;
            Q0 = qSketchRegion(id + "F0", true);
            var Q1;
            Q1=makeQuery(id+"F0.imprint","IMPRINT",FACE,{"disambiguationData":[TD([[makeQuery(id+"F0.imprint","IMPRINT",EDGE,{"derivedFrom":sQuery(id+"F0.wireOp",EDGE,"E12")}),-1.0]])]});
            var Q2;
            Q2=makeQuery(id+"F2.opExtrude","CAP_FACE",FACE,{"disambiguationData":[OSD([sQuery(id+"F0.wireOp",EDGE,"E12"),sQuery(id+"F0.wireOp",EDGE,"E13"),sQuery(id+"F0.wireOp",EDGE,"E14"),sQuery(id+"F0.wireOp",EDGE,"E15"),sQuery(id+"F0.wireOp",EDGE,"E17.filletArc"),sQuery(id+"F0.wireOp",EDGE,"E18.filletArc"),sQuery(id+"F0.wireOp",EDGE,"E19.filletArc"),sQuery(id+"F0.wireOp",EDGE,"E20.filletArc"),sQuery(id+"F0.wireOp",EDGE,"E25.0"),sQuery(id+"F0.wireOp",EDGE,"E25.1"),sQuery(id+"F0.wireOp",EDGE,"E25.2"),sQuery(id+"F0.wireOp",EDGE,"E25.3"),sQuery(id+"F0.wireOp",EDGE,"E25.4"),sQuery(id+"F0.wireOp",EDGE,"E25.5"),sQuery(id+"F0.wireOp",EDGE,"E25.6"),sQuery(id+"F0.wireOp",EDGE,"E25.7")])],"isStart":false});
            extrude(context, id + "F16", {"entities" : qUnion([Q0, Q1]), "endBound" : BoundingType.UP_TO_SURFACE, "depth" : 25 * mm, "endBoundEntityFace" : qUnion([Q2]), "offsetDistance" : 25 * mm});
        }
    });
